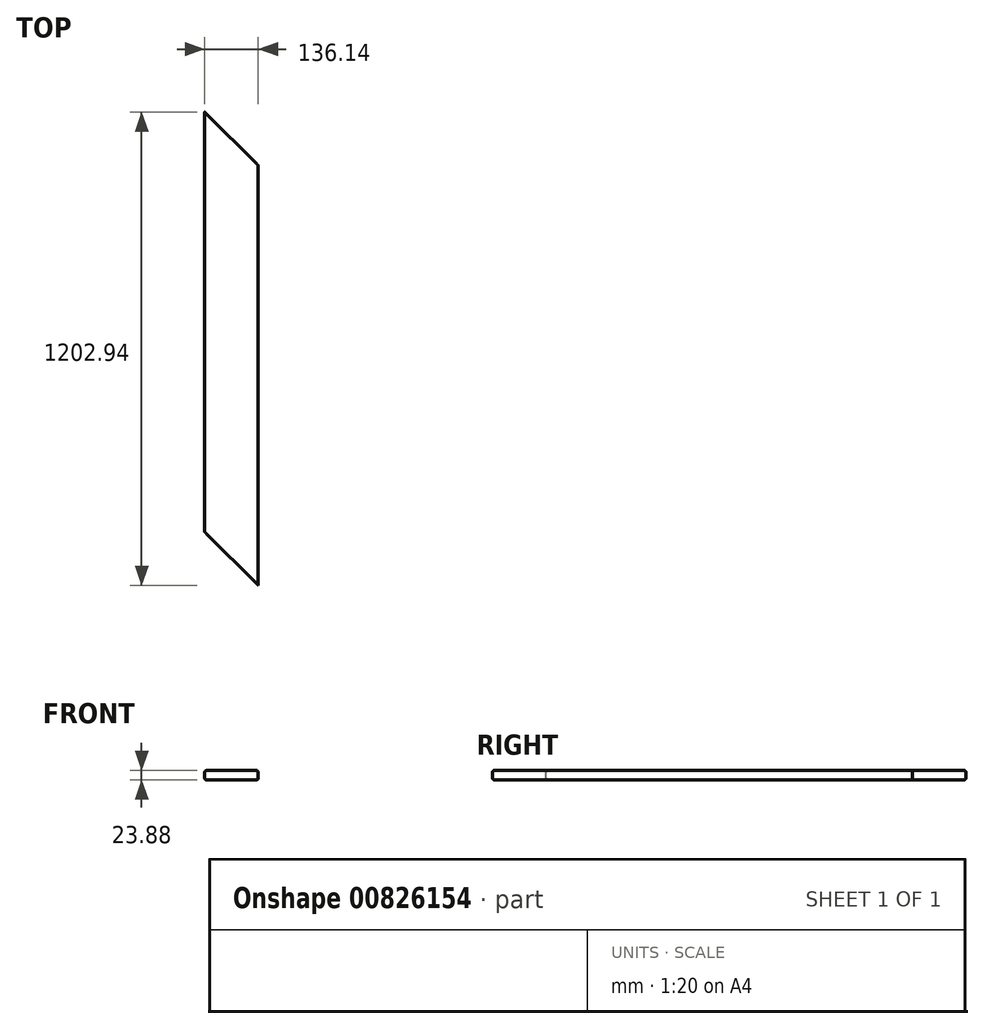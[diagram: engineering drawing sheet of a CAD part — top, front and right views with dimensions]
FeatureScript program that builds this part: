
annotation { "Feature Type Name" : "Feature", "Feature Type Description" : "" }
export const myFeature = defineFeature(function(context is Context, id is Id, definition is map)
    precondition{}
    {
        {
            var Q0;
            Q0=qCreatedBy(makeId("Front.planeOp"),FACE);
            var sketch = newSketch(context, id + "F0", { "sketchPlane" : qUnion([Q0])});
            skLineSegment(sketch, "E0.bottom", {"start": v(-63.25, 11.94) * mm, "end": v(63.25, 11.94) * mm});
            skLineSegment(sketch, "E0.top", {"start": v(-63.25, -11.94) * mm, "end": v(63.25, -11.94) * mm});
            skLineSegment(sketch, "E0.left", {"start": v(-68.07, 7.11) * mm, "end": v(-68.07, -7.11) * mm});
            skLineSegment(sketch, "E0.right", {"start": v(68.07, 7.11) * mm, "end": v(68.07, -7.11) * mm});
            skPoint(sketch, "E0.middle", {"position": v(0, 0) * mm});
            skPoint(sketch, "E1.visualSharp", {"position": v(-68.07, 11.94) * mm});
            skArc(sketch, "E1.filletArc", {"start": v(-63.25, 11.94) * mm, "mid": v(-66.66, 10.52) * mm, "end": v(-68.07, 7.11) * mm});
            skPoint(sketch, "E2.visualSharp", {"position": v(68.07, 11.94) * mm});
            skArc(sketch, "E2.filletArc", {"start": v(68.07, 7.11) * mm, "mid": v(66.66, 10.52) * mm, "end": v(63.25, 11.94) * mm});
            skPoint(sketch, "E3.visualSharp", {"position": v(68.07, -11.94) * mm});
            skArc(sketch, "E3.filletArc", {"start": v(63.25, -11.94) * mm, "mid": v(66.66, -10.52) * mm, "end": v(68.07, -7.11) * mm});
            skPoint(sketch, "E4.visualSharp", {"position": v(-68.07, -11.94) * mm});
            skArc(sketch, "E4.filletArc", {"start": v(-68.07, -7.11) * mm, "mid": v(-66.66, -10.52) * mm, "end": v(-63.25, -11.94) * mm});
            skSolve(sketch);
        }
        {
            var Q0;
            Q0=makeQuery(id+"F0.imprint","IMPRINT",FACE,{"disambiguationData":[TD([[makeQuery(id+"F0.imprint","IMPRINT",EDGE,{"derivedFrom":sQuery(id+"F0.wireOp",EDGE,"E0.bottom")}),-1.0]])]});
            extrude(context, id + "F1", {"entities" : qUnion([Q0]), "endBound" : BoundingType.SYMMETRIC, "depth" : 1202.94 * mm, "offsetDistance" : 25.4 * mm});
        }
        {
            var Q0;
            Q0=makeQuery(id+"F1.opExtrude","SWEPT_FACE",FACE,{"disambiguationData":[OSD([sQuery(id+"F0.wireOp",EDGE,"E0.bottom")])]});
            var sketch = newSketch(context, id + "F2", { "sketchPlane" : qUnion([Q0])});
            skLineSegment(sketch, "E5", {"start": v(68.07, -601.47) * mm, "end": v(-68.07, -601.47) * mm});
            skLineSegment(sketch, "E6", {"start": v(-68.07, -601.47) * mm, "end": v(-68.07, -465.33) * mm});
            skLineSegment(sketch, "E7", {"start": v(-68.07, -465.33) * mm, "end": v(68.07, -601.47) * mm});
            skLineSegment(sketch, "E8", {"start": v(-68.07, 601.47) * mm, "end": v(68.07, 601.47) * mm});
            skLineSegment(sketch, "E9", {"start": v(68.07, 601.47) * mm, "end": v(68.07, 465.33) * mm});
            skLineSegment(sketch, "E10", {"start": v(68.07, 465.33) * mm, "end": v(-68.07, 601.47) * mm});
            skSolve(sketch);
        }
        {
            var Q0;
            Q0=qSketchRegion(id+"F2",true);
            extrude(context, id + "F3", {"entities" : qUnion([Q0]), "operationType" : NewBodyOperationType.REMOVE, "endBound" : BoundingType.THROUGH_ALL, "oppositeDirection" : true, "depth" : 25.4 * mm, "offsetDistance" : 25.4 * mm});
        }
    });
